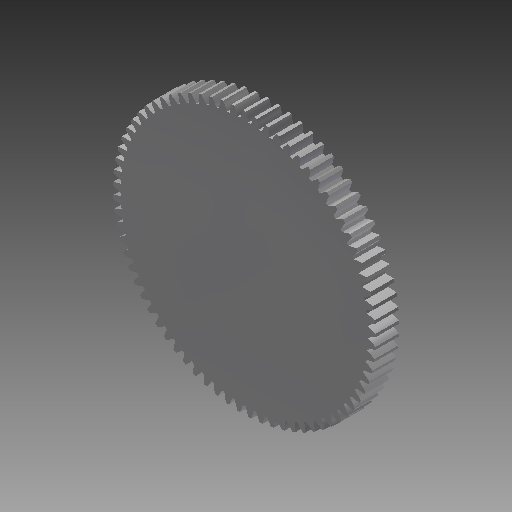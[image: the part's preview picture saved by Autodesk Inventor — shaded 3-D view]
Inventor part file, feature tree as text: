
AUTODESK INVENTOR PART (.ipt)
format: ipt  version: 2019 (Build 230136000, 136)  size: 439,296 bytes
history: native  units: mm (DEFAULTED — no unit token found)
features: plane x3, other x3, sketch x2, extrude x1
ambient origin geometry x8: Origin, YZ Plane, XZ Plane, XY Plane, X Axis, Y Axis, Z Axis, Center Point
bodies: Solid1 (feature_tree)
feature tree (9):
  extrude  "Extrusion1"  Depth=10.0mm TaperAngle=0.0deg
  plane  "Work Plane2"
  plane  "Work Plane8"
  plane  "Work Plane9"
  other  "正齒輪"
  sketch  "Sketch1"  dims[d0=112.5mm d1=10.0mm d2=0.0mm]
  sketch  "Sketch2"  dims[d3=107.647568mm d4=10.0mm d5=0.0mm d16=32.441733mm d17=0.0mm d34=0.430355mm d39=0.0mm d41=0.0mm d43=32.441733mm d46=32.441733mm d47=0.0mm d48=0.0mm]
  other  "Srf1"
  other  "節圓直徑"
